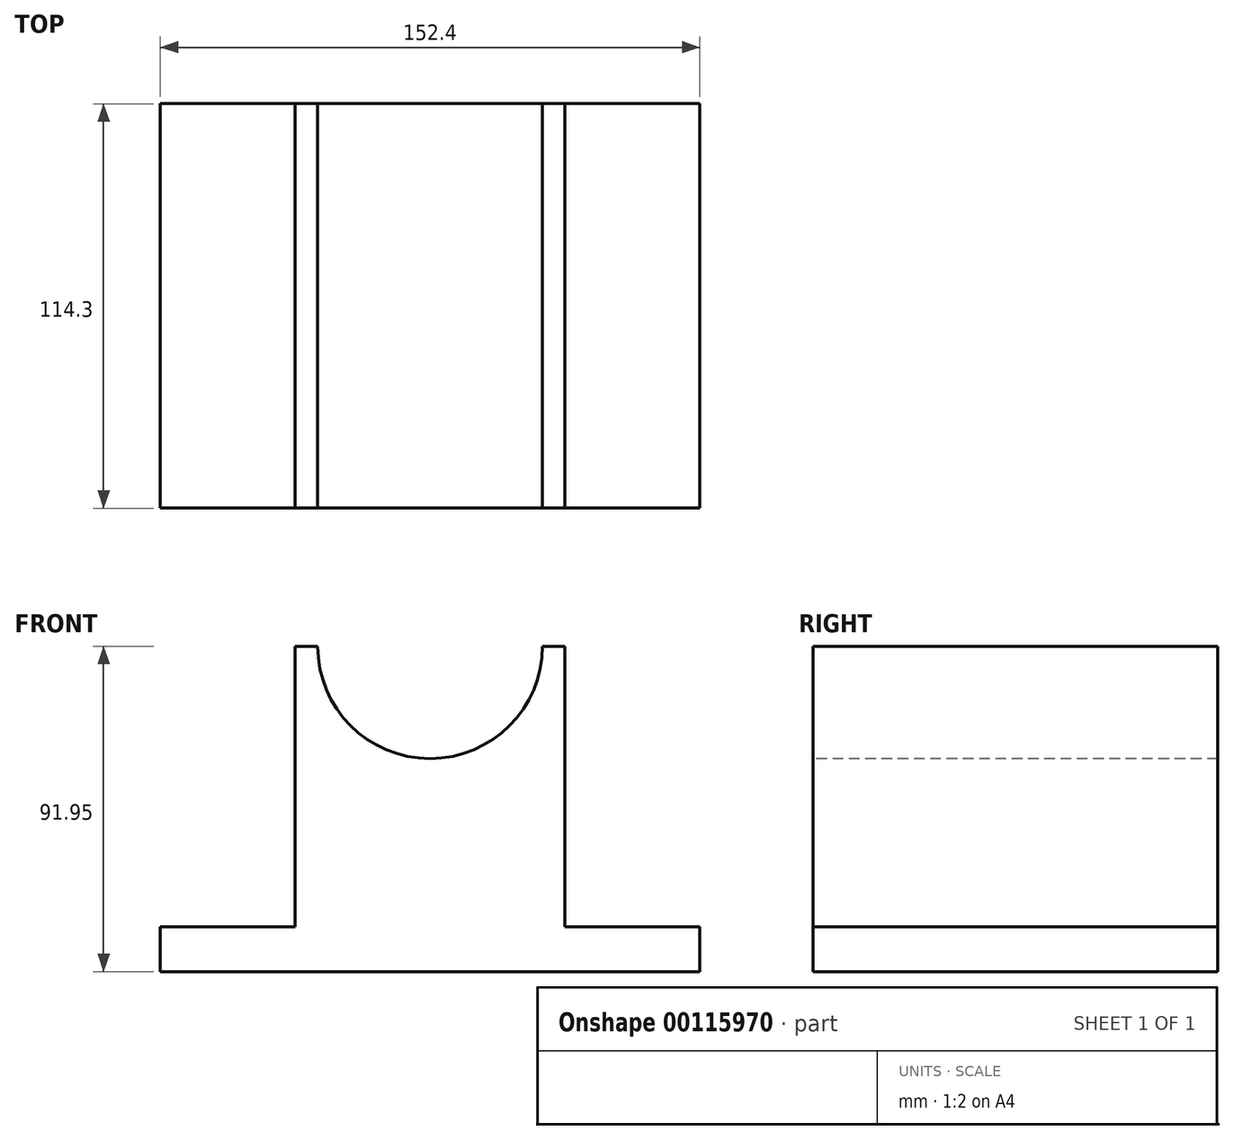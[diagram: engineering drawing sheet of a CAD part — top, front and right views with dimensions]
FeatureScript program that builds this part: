
annotation { "Feature Type Name" : "Feature", "Feature Type Description" : "" }
export const myFeature = defineFeature(function(context is Context, id is Id, definition is map)
    precondition{}
    {
        {
            var Q0;
            Q0=qCreatedBy(makeId("Top.planeOp"),FACE);
            var sketch = newSketch(context, id + "F0", { "sketchPlane" : qUnion([Q0])});
            skLineSegment(sketch, "E0.bottom", {"start": v(-106.22, 76.44) * mm, "end": v(46.18, 76.44) * mm});
            skLineSegment(sketch, "E0.top", {"start": v(-106.22, -37.86) * mm, "end": v(46.18, -37.86) * mm});
            skLineSegment(sketch, "E0.left", {"start": v(-106.22, 76.44) * mm, "end": v(-106.22, -37.86) * mm});
            skLineSegment(sketch, "E0.right", {"start": v(46.18, 76.44) * mm, "end": v(46.18, -37.86) * mm});
            skSolve(sketch);
        }
        {
            var Q0;
            Q0 = qSketchRegion(id + "F0", true);
            extrude(context, id + "F1", {"entities" : qUnion([Q0]), "depth" : 12.7 * mm});
        }
        {
            var Q0;
            Q0=makeQuery(id+"F1.opExtrude","CAP_FACE",FACE,{"disambiguationData":[OSD([sQuery(id+"F0.wireOp",EDGE,"E0.bottom"),sQuery(id+"F0.wireOp",EDGE,"E0.top"),sQuery(id+"F0.wireOp",EDGE,"E0.left"),sQuery(id+"F0.wireOp",EDGE,"E0.right")])],"isStart":false});
            var sketch = newSketch(context, id + "F2", { "sketchPlane" : qUnion([Q0])});
            skLineSegment(sketch, "E1.bottom", {"start": v(-68.12, 76.44) * mm, "end": v(8.08, 76.44) * mm});
            skLineSegment(sketch, "E1.top", {"start": v(-68.12, -37.86) * mm, "end": v(8.08, -37.86) * mm});
            skLineSegment(sketch, "E1.left", {"start": v(-68.12, 76.44) * mm, "end": v(-68.12, -37.86) * mm});
            skLineSegment(sketch, "E1.right", {"start": v(8.08, 76.44) * mm, "end": v(8.08, -37.86) * mm});
            skSolve(sketch);
        }
        {
            var Q0;
            Q0 = qSketchRegion(id + "F2", true);
            extrude(context, id + "F3", {"entities" : qUnion([Q0]), "operationType" : NewBodyOperationType.ADD, "depth" : 79.25 * mm});
        }
        {
            var Q0;
            Q0=makeQuery(id+"F3.boolean.opBoolean","MERGE",FACE,{"derivedFrom":[makeQuery(id+"F1.opExtrude","SWEPT_FACE",FACE,{"disambiguationData":[OSD([sQuery(id+"F0.wireOp",EDGE,"E0.top")])]}),makeQuery(id+"F3.opExtrude","SWEPT_FACE",FACE,{"disambiguationData":[OSD([sQuery(id+"F2.wireOp",EDGE,"E1.top")])]})]});
            var sketch = newSketch(context, id + "F4", { "sketchPlane" : qUnion([Q0])});
            skCircle(sketch, "E2", {"center": v(-30.02, 91.95) * mm, "radius": 31.75 * mm});
            skSolve(sketch);
        }
        {
            var Q0;
            Q0 = qSketchRegion(id + "F4", true);
            extrude(context, id + "F5", {"entities" : qUnion([Q0]), "operationType" : NewBodyOperationType.REMOVE, "endBound" : BoundingType.THROUGH_ALL, "oppositeDirection" : true, "depth" : 25.4 * mm});
        }
    });
